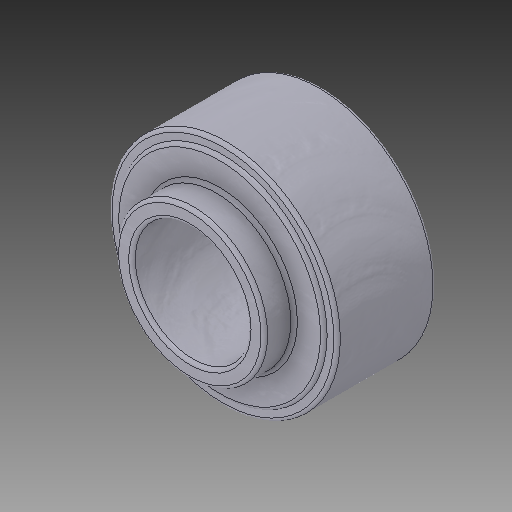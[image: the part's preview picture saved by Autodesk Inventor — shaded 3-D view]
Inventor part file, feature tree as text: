
AUTODESK INVENTOR PART (.ipt)
format: ipt  version: 2019 (Build 230136000, 136)  size: 220,160 bytes
history: native  units: in
note: dims shown in document units (in); Inventor stores cm internally (conversion verified against a paired STEP export)
features: sketch x6, other x3
ambient origin geometry x8: Origin, YZ Plane, XZ Plane, XY Plane, X Axis, Y Axis, Z Axis, Center Point
bodies: Solid1 (feature_tree)
feature tree (9):
  other  "project flange bearing part2_MIR5.ipt"
  other  "Solid1::project flange bearing part2_MIR5.ipt"
  other  "TaggingFeature1"
  sketch  "Sketch1"  dims[d0=0.3937in]
  sketch  "Sketch2"
  sketch  "Sketch3"
  sketch  "Sketch4"
  sketch  "Sketch5"
  sketch  "Sketch6"
